# Revit family: 39601
name_source: partatom
category: Lighting Fixtures
revit_build: Autodesk Revit 2018 (Build: 20170223_1515(x64)
units: mm (PartAtom-declared; Revit-internal decimal feet)

## family parameters
Cut with Voids When Loaded = No
Host = Face
Light Source = Yes
OmniClass Number = 23.80.70.00
OmniClass Title = Lighting
Part Type = Normal
Room Calculation Point = No
Round Connector Dimension = Use Diameter
Shared = No

## types (1)
- 0039601 GRANIT IP65 0-10V 31000LM 840 MB
    00_135W_0-10V = No
    00_135W_DALI = No
    00_180/220W_0-10V = No
    00_180/220W_DALI = No
    00_90W_0-10V = Yes
    00_90W_DALI = No
    Apparent Load = 220 VA
    Assembly Code = D5020200
    AssetType = Fixed
    CHAMFER1_SYL = 143 mm
    ClassificationName = Uniclass2015
    ClassificationValue = EF_70_80
    Color Filter = 16777215
    Cost = 0 $
    DONUT_H_SYL = 147 mm
    DONUT_R1_SYL = 25 mm  [stored 0.082021 ft]
    DR_TOP_SYL = 107 mm  [stored 0.35105 ft]
    DR_WIDTH1_SYL = 61 mm  [stored 0.200131 ft]
    DR_WIDTH_SYL = 58 mm  [stored 0.190289 ft]
    Default Elevation = 1219 mm
    Description = Integrated LED highbay; Black aluminium housing; 31000Lm; 220 W; 141 Lm/W; 4000K; Drive current: 860mA; CRI 80; 55° beam angle; 0-10V dimmable; IP65; IK08; Lifespan L80:B50 90,000 hrs; (D x H) 385 x 181 mm; 1.5 m mains cable; 1.5 m control cable; 1.2 m chain length including hooks.
    Dimming Lamp Color Temperature Shift = <None>
    DocumentationLiterature = http://www.sylvania-lighting.com
    ElectricShockClassification = 141
    Emit Shape Visible in Rendering = No
    Emit from Circle Diameter = 610 mm
    HEIGHT_SYL = 132 mm  [stored 0.433071 ft]
    IfcExportAs = Class I
    IfcExportType = IfcLightFixtureType
    ImpactProtectionIndex = IfcLightFixtureType
    IngressProtection = IfcLightFixtureType
    InputNominalFrequency = 4000
    InputVoltage = 0
    LUM1_HEIGHT_SYL = 31 mm  [stored 0.101706 ft]
    LUM_HEIGHT_SYL = 26 mm
    LUM_TOP_SYL = 107 mm  [stored 0.35105 ft]
    LampColourRenderingIndex = 16500
    LampColourTemperature = LED
    LampMacAdamStep = 80
    LampNominalLuminous = 4000 K
    LightOutputRatio = LED
    LuminaireType = 0
    MID_DR_SYL = 58 mm  [stored 0.190289 ft]
    ManufacturerName = 141 lm/W
    Material = Feilo Sylvania
    Material_1_SYL = <By Category>
    Material_2_SYL = <By Category>
    Material_3_SYL = <By Category>
    Material_4_SYL = <By Category>
    Model = Granit IP65 0-10V 31000lm 840 MB
    ModelNumber = 0039601
    ModelReference = Granit IP65 0-10V 31000lm 840 MB
    Name = Granit IP65 0-10V 31000lm 840 MB
    NominalDepth = 308 mm
    NominalHeight = 166 mm
    NominalLength = 385 mm
    Photometric Web File = 0039601.ies
    PowerConsumption = Lighting
    PowerFactor = 0.95
    RAD1_SYL = 154 mm  [stored 0.505249 ft]
    RING_BOTT_SYL = 61 mm  [stored 0.200131 ft]
    RING_SYL = 65 mm  [stored 0.213255 ft]
    RING_TOP_SYL = 66 mm  [stored 0.216535 ft]
    SENSOR_HEIGHT_SYL = 3 mm  [stored 0.00984252 ft]
    SENSOR_WIDTH_SYL = 40 mm  [stored 0.131234 ft]
    TOP_D_SYL = 15 mm  [stored 0.0492126 ft]
    Tilt Angle = -90.00°
    Type Image = <None>
    TypeName = Granit IP65 0-10V 31000lm 840 MB
    URL = 1
    Voltage = 0 V
    WarrantyDescription = http://www.sylvania-lighting.com

note: [stored X ft] marks values corroborated as IEEE doubles in the binary element streams (Revit-internal decimal feet)

## geometry (parser evidence)
native form markers: Sweep x3
no freeform markers — native parametric forms only
